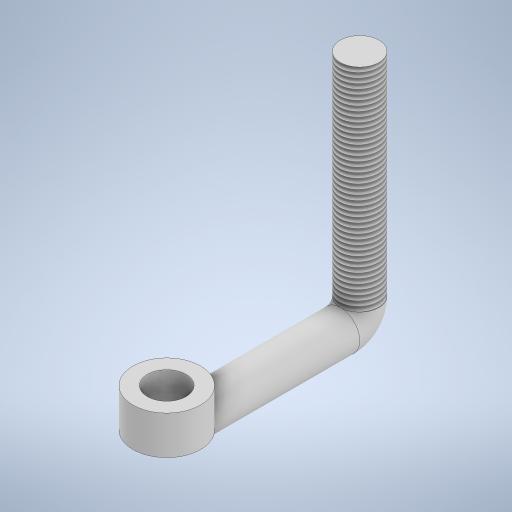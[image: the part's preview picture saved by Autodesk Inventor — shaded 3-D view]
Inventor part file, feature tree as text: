
AUTODESK INVENTOR PART (.ipt)
format: ipt  version: 2024 (Build 280153000, 153)  size: 303,616 bytes
history: native  units: in
note: dims shown in document units (in); Inventor stores cm internally (conversion verified against a paired STEP export)
features: sketch x5, extrude x3, sweep x1, thread x1
ambient origin geometry x8: Origin, YZ Plane, XZ Plane, XY Plane, X Axis, Y Axis, Z Axis, Center Point
bodies: Solid1 (feature_tree)
feature tree (10):
  sweep  "Sweep1"
  thread  "Thread1"  [1 undecoded]
  extrude  "Extrusion1"  TaperAngle=0.0deg  [1 undecoded]
  extrude  "Extrusion2"  Depth=1.378in
  extrude  "Extrusion3"  Depth=0.7874in
  sketch  "Sketch1"  dims[d0=0.7874in d1=3.937in d2=4.7244in]
  sketch  "Sketch2"  dims[d3=0.3937in d4=0.0in d5=0.0in]
  sketch  "Sketch3"  dims[d6=2.7559in d7=0.0in d8=1.378in]
  sketch  "Sketch4"  dims[d9=0.7874in d10=0.0in d11=0.7874in]
  sketch  "Sketch5"  dims[d12=0.0in d13=0.0in d14=0.3937in d15=0.0in]
note: 2 required parameter values undecoded (feature->parameter linkage not recoverable at this tier; creation-order binding heuristic only, values carry confidence <= 0.55)
